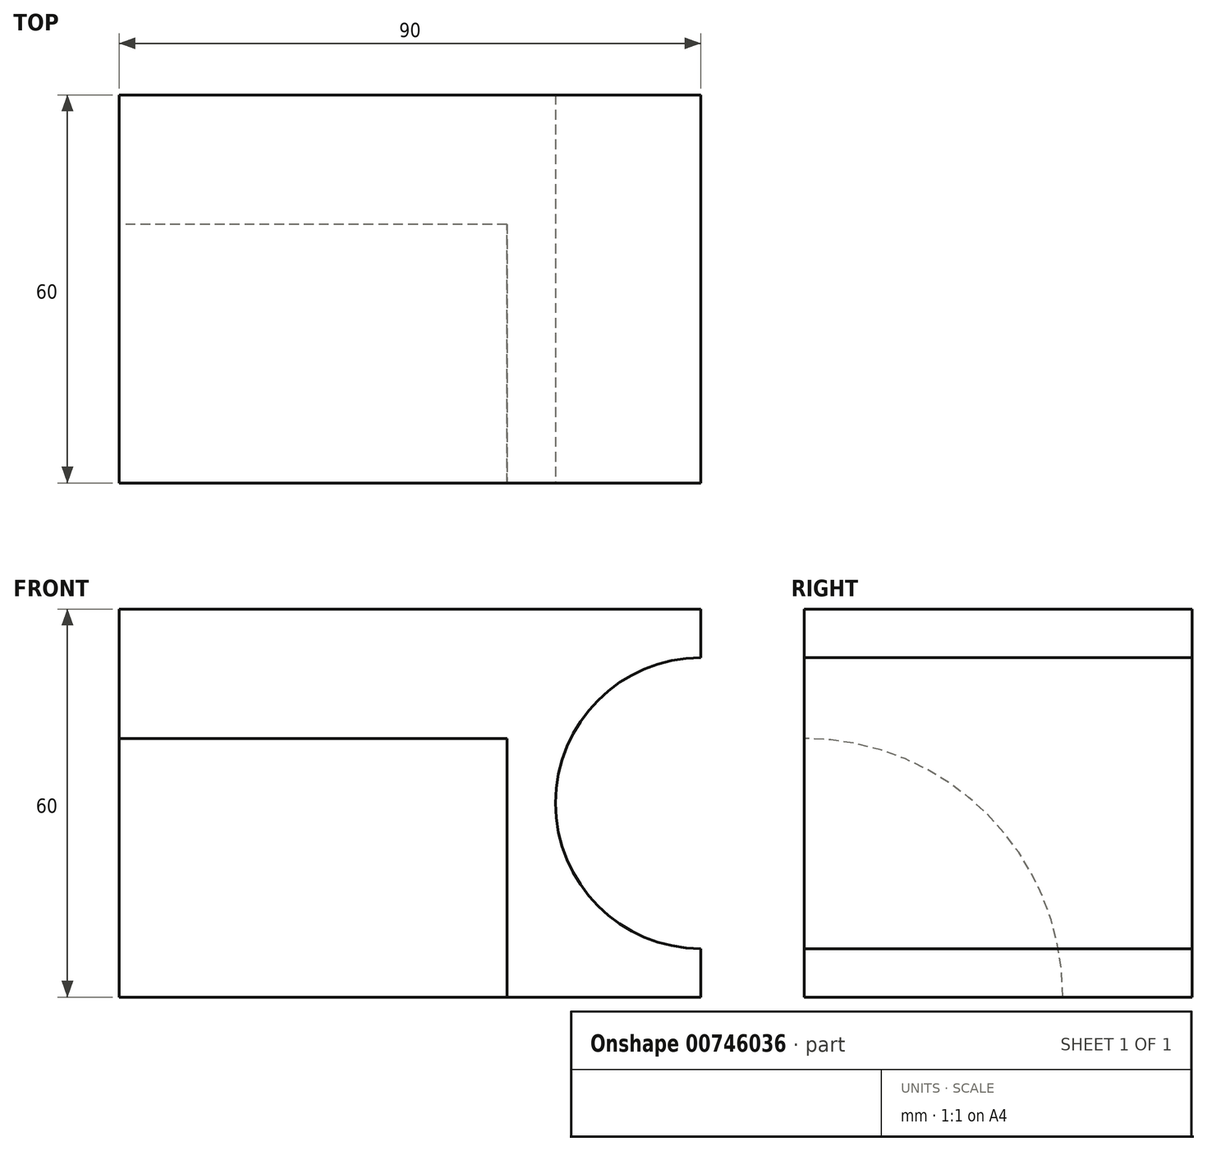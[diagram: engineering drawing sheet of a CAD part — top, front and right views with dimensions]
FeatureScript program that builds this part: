
annotation { "Feature Type Name" : "Feature", "Feature Type Description" : "" }
export const myFeature = defineFeature(function(context is Context, id is Id, definition is map)
    precondition{}
    {
        {
            var Q0;
            Q0=qCreatedBy(makeId("Front.planeOp"),FACE);
            var sketch = newSketch(context, id + "F0", { "sketchPlane" : qUnion([Q0])});
            skLineSegment(sketch, "E0.bottom", {"start": v(0, 0) * mm, "end": v(90, 0) * mm});
            skLineSegment(sketch, "E0.top", {"start": v(0, 60) * mm, "end": v(90, 60) * mm});
            skLineSegment(sketch, "E0.left", {"start": v(0, 0) * mm, "end": v(0, 60) * mm});
            skLineSegment(sketch, "E0.right", {"start": v(90, 0) * mm, "end": v(90, 60) * mm});
            skSolve(sketch);
        }
        {
            var Q0;
            Q0 = qSketchRegion(id + "F0", true);
            extrude(context, id + "F1", {"entities" : qUnion([Q0]), "depth" : 60 * mm, "offsetDistance" : 25 * mm});
        }
        {
            var Q0;
            Q0=makeQuery(id+"F1.opExtrude","CAP_FACE",FACE,{"disambiguationData":[OSD([sQuery(id+"F0.wireOp",EDGE,"E0.bottom"),sQuery(id+"F0.wireOp",EDGE,"E0.top"),sQuery(id+"F0.wireOp",EDGE,"E0.left"),sQuery(id+"F0.wireOp",EDGE,"E0.right")])],"isStart":false});
            var sketch = newSketch(context, id + "F2", { "sketchPlane" : qUnion([Q0])});
            skCircle(sketch, "E1", {"center": v(90, 30) * mm, "radius": 22.5 * mm});
            skSolve(sketch);
        }
        {
            var Q0;
            {var subQ0=sQuery(id+"F2.wireOp",EDGE,"E1");var subQ1=makeQuery(id+"F1.opExtrude","CAP_EDGE",EDGE,{"disambiguationData":[OSD([sQuery(id+"F0.wireOp",EDGE,"E0.right")])],"isStart":false});var subQ2=makeQuery(id+"F2.imprint","INTERSECT",VERTEX,{"disambiguationData":[OD(0.0)],"derivedFrom":[subQ1,subQ0]});Q0=makeQuery(id+"F2.imprint","IMPRINT",FACE,{"disambiguationData":[TD([[makeQuery(id+"F2.imprint","IMPRINT",EDGE,{"disambiguationData":[TD([[subQ2,1.0]])],"derivedFrom":subQ0}),1.0]])]});}
            extrude(context, id + "F3", {"entities" : qUnion([Q0]), "operationType" : NewBodyOperationType.REMOVE, "endBound" : BoundingType.THROUGH_ALL, "oppositeDirection" : true, "depth" : 25 * mm, "offsetDistance" : 25 * mm});
        }
        {
            var Q0;
            Q0=makeQuery(id+"F1.opExtrude","SWEPT_FACE",FACE,{"disambiguationData":[OSD([sQuery(id+"F0.wireOp",EDGE,"E0.left")])]});
            var sketch = newSketch(context, id + "F4", { "sketchPlane" : qUnion([Q0])});
            skCircle(sketch, "E2", {"center": v(60, 0) * mm, "radius": 40 * mm});
            skSolve(sketch);
        }
        {
            var Q0;
            Q0 = qSketchRegion(id + "F4", true);
            extrude(context, id + "F5", {"entities" : qUnion([Q0]), "operationType" : NewBodyOperationType.REMOVE, "oppositeDirection" : true, "depth" : 60 * mm, "offsetDistance" : 25 * mm});
        }
    });
